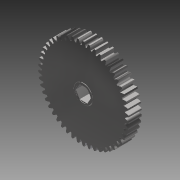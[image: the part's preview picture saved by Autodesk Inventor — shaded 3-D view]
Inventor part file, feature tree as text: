
AUTODESK INVENTOR PART (.ipt)
format: ipt  version: 2014 (Build 180170000, 170)  size: 389,632 bytes
history: native  units: mm (DEFAULTED — no unit token found)
features: plane x4, fillet x4, sketch x4, extrude x3, other x3, mirror x1
ambient origin geometry x8: Origin, YZ Plane, XZ Plane, XY Plane, X Axis, Y Axis, Z Axis, Center Point
bodies: Solid1 (feature_tree)
feature tree (19):
  extrude  "Extrusion1"  Depth=9.525mm TaperAngle=0.0deg
  plane  "Work Plane1"
  plane  "Work Plane2"
  plane  "Work Plane3"
  other  "Spur Gear"
  extrude  "Extrusion2"  Depth=76.2mm TaperAngle=0.0deg
  extrude  "Extrusion3"  TaperAngle=0.0deg  [1 undecoded]
  fillet  "Fillet1"  Radius=62.23mm
  fillet  "Fillet2"  [1 undecoded]
  plane  "Work Plane4"
  mirror  "Mirror1"
  fillet  "Fillet3"  Radius=9.5758mm
  fillet  "Fillet4"  Radius=25.4mm
  sketch  "Sketch1"  dims[d0=66.04mm d1=9.525mm d2=0.0mm]
  sketch  "Sketch2"  dims[d3=63.5mm d4=76.2mm d5=0.0mm]
  other  "Srf1"
  sketch  "Sketch3"  dims[d6=0.0mm d7=0.628319mm d9=0.0mm d14=0.0mm d15=62.23mm d16=0.0mm]
  sketch  "Sketch4"  dims[d17=0.0mm d18=0.0mm d19=62.23mm d20=9.5758mm d21=25.4mm d22=0.0mm d23=1.27mm d25=0.3175mm d26=0.0mm d27=0.3175mm d28=0.254mm d29=0.3175mm d30=0.254mm]
  other  "Pitch Diameter"
note: 2 required parameter values undecoded (feature->parameter linkage not recoverable at this tier; creation-order binding heuristic only, values carry confidence <= 0.55)
